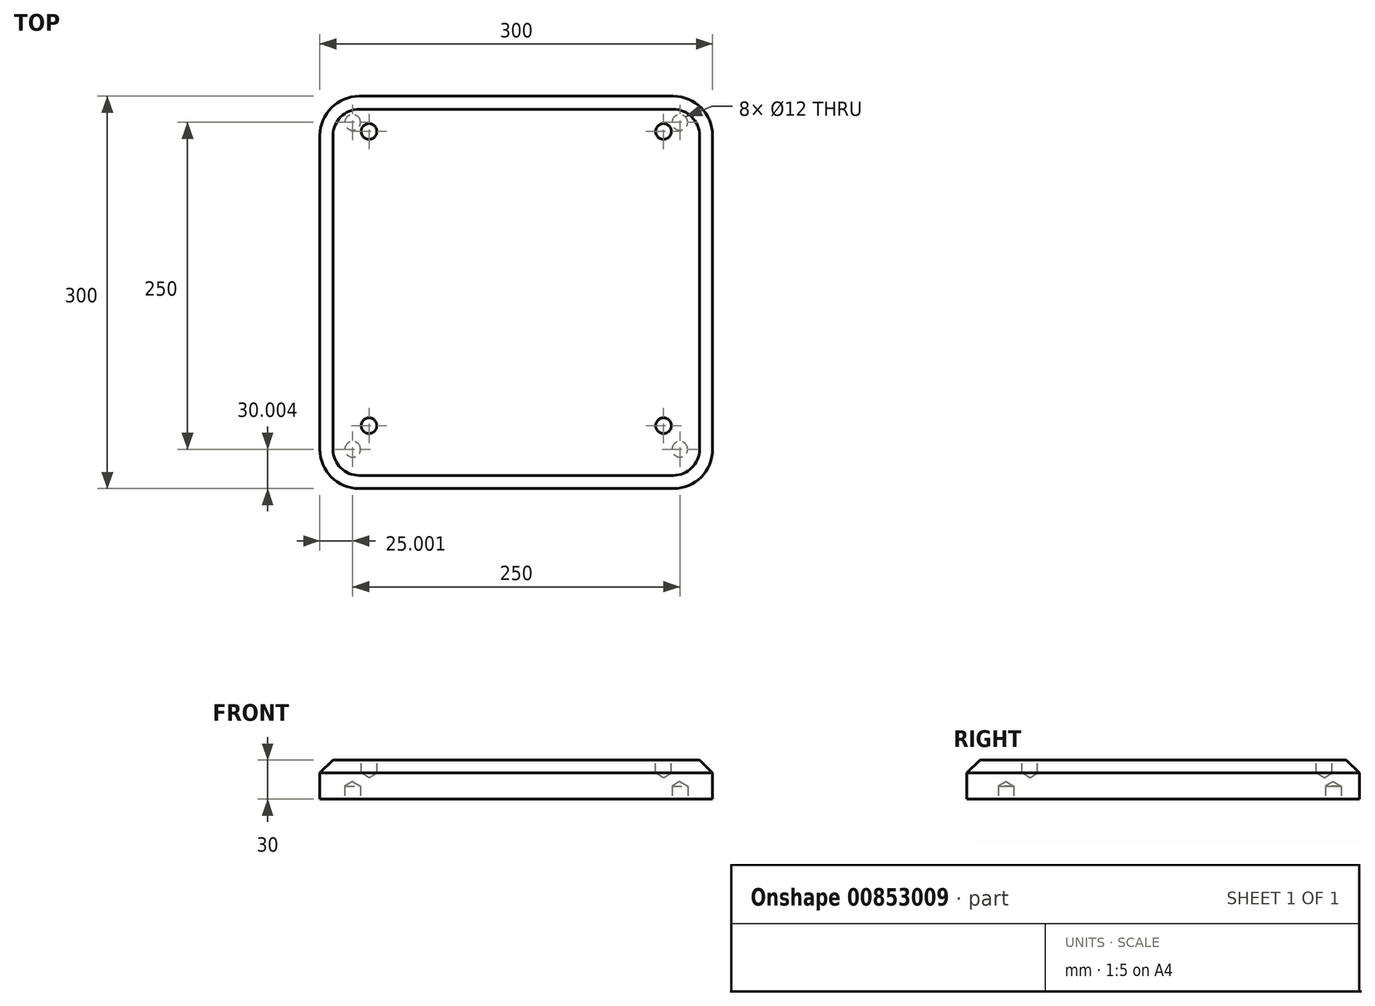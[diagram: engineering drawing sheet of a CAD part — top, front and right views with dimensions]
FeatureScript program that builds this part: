
annotation { "Feature Type Name" : "Feature", "Feature Type Description" : "" }
export const myFeature = defineFeature(function(context is Context, id is Id, definition is map)
    precondition{}
    {
        {
            var Q0;
            Q0=qCreatedBy(makeId("Top.planeOp"),FACE);
            var sketch = newSketch(context, id + "F0", { "sketchPlane" : qUnion([Q0])});
            skLineSegment(sketch, "E0.bottom", {"start": v(-144.12, 182.37) * mm, "end": v(95.88, 182.37) * mm});
            skLineSegment(sketch, "E0.top", {"start": v(-144.12, -117.63) * mm, "end": v(95.88, -117.63) * mm});
            skLineSegment(sketch, "E0.left", {"start": v(-174.12, 152.37) * mm, "end": v(-174.12, -87.63) * mm});
            skLineSegment(sketch, "E0.right", {"start": v(125.88, 152.37) * mm, "end": v(125.88, -87.63) * mm});
            skPoint(sketch, "E1.visualSharp", {"position": v(-174.12, 182.37) * mm});
            skArc(sketch, "E1.filletArc", {"start": v(-144.12, 182.37) * mm, "mid": v(-165.33, 173.59) * mm, "end": v(-174.12, 152.37) * mm});
            skPoint(sketch, "E2.visualSharp", {"position": v(125.88, 182.37) * mm});
            skArc(sketch, "E2.filletArc", {"start": v(125.88, 152.37) * mm, "mid": v(117.1, 173.59) * mm, "end": v(95.88, 182.37) * mm});
            skPoint(sketch, "E3.visualSharp", {"position": v(-174.12, -117.63) * mm});
            skArc(sketch, "E3.filletArc", {"start": v(-174.12, -87.63) * mm, "mid": v(-165.33, -108.84) * mm, "end": v(-144.12, -117.63) * mm});
            skPoint(sketch, "E4.visualSharp", {"position": v(125.88, -117.63) * mm});
            skArc(sketch, "E4.filletArc", {"start": v(95.88, -117.63) * mm, "mid": v(117.1, -108.84) * mm, "end": v(125.88, -87.63) * mm});
            skSolve(sketch);
        }
        {
            var Q0;
            Q0=makeQuery(id+"F0.imprint","IMPRINT",FACE,{"disambiguationData":[TD([[makeQuery(id+"F0.imprint","IMPRINT",EDGE,{"derivedFrom":sQuery(id+"F0.wireOp",EDGE,"E0.bottom")}),-1.0]])]});
            extrude(context, id + "F1", {"entities" : qUnion([Q0]), "depth" : 30 * mm, "offsetDistance" : 25 * mm});
        }
        {
            var Q0;
            Q0=makeQuery(id+"F1.opExtrude","CAP_FACE",FACE,{"disambiguationData":[OSD([sQuery(id+"F0.wireOp",EDGE,"E0.bottom"),sQuery(id+"F0.wireOp",EDGE,"E0.top"),sQuery(id+"F0.wireOp",EDGE,"E0.left"),sQuery(id+"F0.wireOp",EDGE,"E0.right"),sQuery(id+"F0.wireOp",EDGE,"E1.filletArc"),sQuery(id+"F0.wireOp",EDGE,"E2.filletArc"),sQuery(id+"F0.wireOp",EDGE,"E3.filletArc"),sQuery(id+"F0.wireOp",EDGE,"E4.filletArc")])],"isStart":false});
            var sketch = newSketch(context, id + "F2", { "sketchPlane" : qUnion([Q0])});
            skCircle(sketch, "E5", {"center": v(-136.62, -69.55) * mm, "radius": 6 * mm});
            skCircle(sketch, "E6", {"center": v(-136.62, 155.45) * mm, "radius": 6 * mm});
            skCircle(sketch, "E7", {"center": v(88.38, 155.45) * mm, "radius": 6 * mm});
            skCircle(sketch, "E8", {"center": v(88.38, -69.55) * mm, "radius": 6 * mm});
            skSolve(sketch);
        }
        {
            var Q0;
            Q0=sQuery(id+"F2.wireOp",VERTEX,"E6.center");
            var Q1;
            Q1=sQuery(id+"F2.wireOp",VERTEX,"E7.center");
            var Q2;
            Q2=sQuery(id+"F2.wireOp",VERTEX,"E5.center");
            var Q3;
            Q3=sQuery(id+"F2.wireOp",VERTEX,"E8.center");
            var Q4;
            Q4=makeQuery(id+"F1.opExtrude","SWEPT_BODY",BODY,{"disambiguationData":[OSD([sQuery(id+"F0.wireOp",EDGE,"E0.bottom"),sQuery(id+"F0.wireOp",EDGE,"E0.top"),sQuery(id+"F0.wireOp",EDGE,"E0.left"),sQuery(id+"F0.wireOp",EDGE,"E0.right"),sQuery(id+"F0.wireOp",EDGE,"E1.filletArc"),sQuery(id+"F0.wireOp",EDGE,"E2.filletArc"),sQuery(id+"F0.wireOp",EDGE,"E3.filletArc"),sQuery(id+"F0.wireOp",EDGE,"E4.filletArc")])]});
            hole(context, id + "F3", {"style" : HoleStyle.SIMPLE, "endStyle" : HoleEndStyle.BLIND, "holeDiameter" : 12 * mm, "majorDiameter" : 5 * mm, "holeDepth" : 10 * mm, "isTappedThrough" : true, "tappedDepth" : 12 * mm, "tapClearance" : 3, "locations" : qUnion([Q0, Q1, Q2, Q3]), "scope" : qUnion([Q4])});
        }
        {
            var Q0;
            Q0=makeQuery(id+"F1.opExtrude","CAP_EDGE",EDGE,{"disambiguationData":[OSD([sQuery(id+"F0.wireOp",EDGE,"E1.filletArc")])],"isStart":false});
            var Q1;
            Q1=makeQuery(id+"F1.opExtrude","CAP_EDGE",EDGE,{"disambiguationData":[OSD([sQuery(id+"F0.wireOp",EDGE,"E0.left")])],"isStart":false});
            var Q2;
            Q2=makeQuery(id+"F1.opExtrude","CAP_EDGE",EDGE,{"disambiguationData":[OSD([sQuery(id+"F0.wireOp",EDGE,"E3.filletArc")])],"isStart":false});
            var Q3;
            Q3=makeQuery(id+"F1.opExtrude","CAP_EDGE",EDGE,{"disambiguationData":[OSD([sQuery(id+"F0.wireOp",EDGE,"E0.top")])],"isStart":false});
            var Q4;
            Q4=makeQuery(id+"F1.opExtrude","CAP_EDGE",EDGE,{"disambiguationData":[OSD([sQuery(id+"F0.wireOp",EDGE,"E4.filletArc")])],"isStart":false});
            var Q5;
            Q5=makeQuery(id+"F1.opExtrude","CAP_EDGE",EDGE,{"disambiguationData":[OSD([sQuery(id+"F0.wireOp",EDGE,"E0.right")])],"isStart":false});
            var Q6;
            Q6=makeQuery(id+"F1.opExtrude","CAP_EDGE",EDGE,{"disambiguationData":[OSD([sQuery(id+"F0.wireOp",EDGE,"E2.filletArc")])],"isStart":false});
            var Q7;
            Q7=makeQuery(id+"F1.opExtrude","CAP_EDGE",EDGE,{"disambiguationData":[OSD([sQuery(id+"F0.wireOp",EDGE,"E0.bottom")])],"isStart":false});
            chamfer(context, id + "F4", {"entities" : qUnion([Q0, Q1, Q2, Q3, Q4, Q5, Q6, Q7]), "chamferType" : ChamferType.OFFSET_ANGLE, "width" : 10 * mm, "oppositeDirection" : false, "angle" : 45 * degree, "tangentPropagation" : true});
        }
        {
            var Q0;
            Q0=makeQuery(id+"F1.opExtrude","CAP_FACE",FACE,{"disambiguationData":[OSD([sQuery(id+"F0.wireOp",EDGE,"E0.bottom"),sQuery(id+"F0.wireOp",EDGE,"E0.top"),sQuery(id+"F0.wireOp",EDGE,"E0.left"),sQuery(id+"F0.wireOp",EDGE,"E0.right"),sQuery(id+"F0.wireOp",EDGE,"E1.filletArc"),sQuery(id+"F0.wireOp",EDGE,"E2.filletArc"),sQuery(id+"F0.wireOp",EDGE,"E3.filletArc"),sQuery(id+"F0.wireOp",EDGE,"E4.filletArc")])],"isStart":true});
            var sketch = newSketch(context, id + "F5", { "sketchPlane" : qUnion([Q0])});
            skCircle(sketch, "E9", {"center": v(-149.12, 87.63) * mm, "radius": 6 * mm});
            skCircle(sketch, "E10", {"center": v(100.88, 87.63) * mm, "radius": 6 * mm});
            skCircle(sketch, "E11", {"center": v(-149.12, -162.37) * mm, "radius": 6 * mm});
            skCircle(sketch, "E12", {"center": v(100.88, -162.37) * mm, "radius": 6 * mm});
            skSolve(sketch);
        }
        {
            var Q0;
            Q0=sQuery(id+"F5.wireOp",VERTEX,"E9.center");
            var Q1;
            Q1=sQuery(id+"F5.wireOp",VERTEX,"E10.center");
            var Q2;
            Q2=sQuery(id+"F5.wireOp",VERTEX,"E11.center");
            var Q3;
            Q3=sQuery(id+"F5.wireOp",VERTEX,"E12.center");
            var Q4;
            Q4=makeQuery(id+"F1.opExtrude","SWEPT_BODY",BODY,{"disambiguationData":[OSD([sQuery(id+"F0.wireOp",EDGE,"E0.bottom"),sQuery(id+"F0.wireOp",EDGE,"E0.top"),sQuery(id+"F0.wireOp",EDGE,"E0.left"),sQuery(id+"F0.wireOp",EDGE,"E0.right"),sQuery(id+"F0.wireOp",EDGE,"E1.filletArc"),sQuery(id+"F0.wireOp",EDGE,"E2.filletArc"),sQuery(id+"F0.wireOp",EDGE,"E3.filletArc"),sQuery(id+"F0.wireOp",EDGE,"E4.filletArc")])]});
            hole(context, id + "F6", {"style" : HoleStyle.SIMPLE, "endStyle" : HoleEndStyle.BLIND, "holeDiameter" : 12 * mm, "majorDiameter" : 5 * mm, "holeDepth" : 10 * mm, "isTappedThrough" : true, "tappedDepth" : 12 * mm, "tapClearance" : 3, "locations" : qUnion([Q0, Q1, Q2, Q3]), "scope" : qUnion([Q4])});
        }
    });
